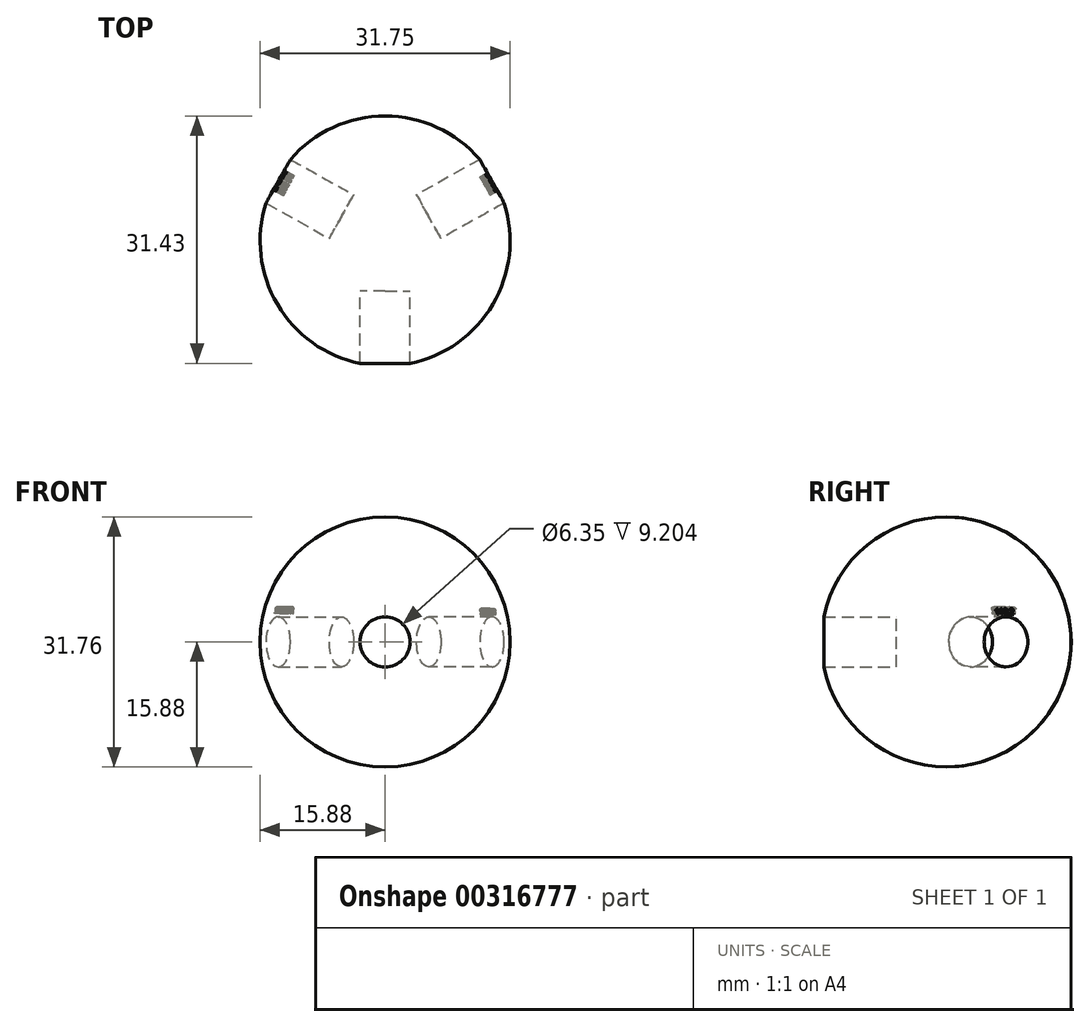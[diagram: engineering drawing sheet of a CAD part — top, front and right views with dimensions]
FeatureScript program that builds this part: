
annotation { "Feature Type Name" : "Feature", "Feature Type Description" : "" }
export const myFeature = defineFeature(function(context is Context, id is Id, definition is map)
    precondition{}
    {
        {
            var Q0;
            Q0=qCreatedBy(makeId("Front.planeOp"),FACE);
            var sketch = newSketch(context, id + "F0", { "sketchPlane" : qUnion([Q0])});
            skArc(sketch, "E0", {"start": v(0, 15.88) * mm, "mid": v(-15.88, 0) * mm, "end": v(0, -15.88) * mm});
            skLineSegment(sketch, "E1", {"start": v(0, 15.88) * mm, "end": v(0, -15.88) * mm});
            skSolve(sketch);
        }
        {
            var Q0;
            Q0=qCreatedBy(makeId("Top.planeOp"),FACE);
            var sketch = newSketch(context, id + "F1", { "sketchPlane" : qUnion([Q0])});
            skCircle(sketch, "E2", {"center": v(0, 0) * mm, "radius": 15.88 * mm});
            skSolve(sketch);
        }
        {
            var Q0;
            Q0=makeQuery(id+"F0.imprint","IMPRINT",FACE,{"disambiguationData":[TD([[makeQuery(id+"F0.imprint","IMPRINT",EDGE,{"derivedFrom":sQuery(id+"F0.wireOp",EDGE,"E0")}),1.0]])]});
            var Q1;
            Q1=sQuery(id+"F1.wireOp",EDGE,"E2");
            revolve(context, id + "F2", {"entities" : qUnion([Q0]), "axis" : qUnion([Q1]), "revolveType" : RevolveType.FULL});
        }
        {
            var Q0;
            Q0=qCreatedBy(makeId("Front.planeOp"),FACE);
            cPlane(context, id + "F3", {"entities" : qUnion([Q0]), "cplaneType" : CPlaneType.OFFSET, "offset" : 6.35 * mm, "width" : 152.4 * mm, "height" : 152.4 * mm});
        }
        {
            var Q0;
            Q0=qCreatedBy(id+"F3.planeOp",FACE);
            var sketch = newSketch(context, id + "F4", { "sketchPlane" : qUnion([Q0])});
            skCircle(sketch, "E3", {"center": v(0, 0) * mm, "radius": 3.18 * mm});
            skSolve(sketch);
        }
        {
            var Q0;
            Q0=qSketchRegion(id+"F4",true);
            extrude(context, id + "F5", {"entities" : qUnion([Q0]), "depth" : 25.4 * mm});
        }
        {
            var Q0;
            Q0=qCreatedBy(makeId("Right.planeOp"),FACE);
            var sketch = newSketch(context, id + "F6", { "sketchPlane" : qUnion([Q0])});
            skLineSegment(sketch, "E4", {"start": v(0, 67.47) * mm, "end": v(0, -53.83) * mm, "construction": true});
            skSolve(sketch);
        }
        {
            var Q0;
            Q0=makeQuery(id+"F5.opExtrude","SWEPT_BODY",BODY,{"disambiguationData":[OSD([sQuery(id+"F4.wireOp",EDGE,"E3")])]});
            var Q1;
            Q1=sQuery(id+"F6.wireOp",EDGE,"E4");
            transform(context, id + "F7", {"entities" : qUnion([Q0]), "transformType" : TransformType.ROTATION, "transformAxis" : qUnion([Q1]), "angle" : 119.2 * degree, "makeCopy" : true});
        }
        {
            var Q0;
            Q0=makeQuery(id+"F5.opExtrude","SWEPT_BODY",BODY,{"disambiguationData":[OSD([sQuery(id+"F4.wireOp",EDGE,"E3")])]});
            var Q1;
            Q1=sQuery(id+"F6.wireOp",EDGE,"E4");
            transform(context, id + "F8", {"entities" : qUnion([Q0]), "transformType" : TransformType.ROTATION, "transformAxis" : qUnion([Q1]), "angle" : 119.2 * degree, "oppositeDirection" : true, "makeCopy" : true});
        }
        {
            var Q0;
            Q0=makeQuery(id+"F7.opPattern","COPY",FACE,{"derivedFrom":makeQuery(id+"F5.opExtrude","CAP_FACE",FACE,{"disambiguationData":[OSD([sQuery(id+"F4.wireOp",EDGE,"E3")])],"isStart":false}),"instanceName":"1"});
            cPlane(context, id + "F9", {"entities" : qUnion([Q0]), "cplaneType" : CPlaneType.OFFSET, "offset" : 15.21 * mm, "oppositeDirection" : true, "width" : 152.4 * mm, "height" : 152.4 * mm});
        }
        {
            var Q0;
            Q0=qCreatedBy(id+"F9.planeOp",FACE);
            var sketch = newSketch(context, id + "F10", { "sketchPlane" : qUnion([Q0])});
            skText(sketch, "E5", { "text": "119.2", "fontName": "OpenSans-Bold.ttf"});
            const initialGuessF10  = {"E5": [-0.00169, 0.00362, 1, 0, 0.00084]};
            skSetInitialGuess(sketch, initialGuessF10);
            skSolve(sketch);
        }
        {
            var Q0;
            Q0 = qSketchRegion(id + "F10", true);
            extrude(context, id + "F11", {"entities" : qUnion([Q0]), "operationType" : NewBodyOperationType.REMOVE, "oppositeDirection" : true, "depth" : 2.41 * mm});
        }
        {
            var Q0;
            Q0=makeQuery(id+"F8.opPattern","COPY",FACE,{"derivedFrom":makeQuery(id+"F5.opExtrude","CAP_FACE",FACE,{"disambiguationData":[OSD([sQuery(id+"F4.wireOp",EDGE,"E3")])],"isStart":false}),"instanceName":"1"});
            cPlane(context, id + "F12", {"entities" : qUnion([Q0]), "cplaneType" : CPlaneType.OFFSET, "offset" : 15.14 * mm, "oppositeDirection" : true, "width" : 152.4 * mm, "height" : 152.4 * mm});
        }
        {
            var Q0;
            Q0=qCreatedBy(id+"F12.planeOp",FACE);
            var sketch = newSketch(context, id + "F13", { "sketchPlane" : qUnion([Q0])});
            skText(sketch, "E6", { "text": "119.2", "fontName": "OpenSans-Bold.ttf"});
            const initialGuessF13  = {"E6": [-0.00147, 0.00348, 1, 0, 0.00076]};
            skSetInitialGuess(sketch, initialGuessF13);
            skSolve(sketch);
        }
        {
            var Q0;
            Q0 = qSketchRegion(id + "F13", true);
            extrude(context, id + "F14", {"entities" : qUnion([Q0]), "operationType" : NewBodyOperationType.REMOVE, "oppositeDirection" : true, "depth" : 2.1 * mm});
        }
        {
            var Q0;
            Q0=makeQuery(id+"F7.opPattern","COPY",BODY,{"derivedFrom":makeQuery(id+"F5.opExtrude","SWEPT_BODY",BODY,{"disambiguationData":[OSD([sQuery(id+"F4.wireOp",EDGE,"E3")])]}),"instanceName":"1"});
            var Q1;
            Q1=makeQuery(id+"F2.opRevolve","SWEPT_BODY",BODY,{"disambiguationData":[OSD([sQuery(id+"F0.wireOp",EDGE,"E0"),sQuery(id+"F0.wireOp",EDGE,"E1")])]});
            booleanBodies(context, id + "F15", {"operationType" : BooleanOperationType.SUBTRACTION, "tools" : qUnion([Q0]), "targets" : qUnion([Q1])});
        }
        {
            var Q0;
            Q0=makeQuery(id+"F8.opPattern","COPY",BODY,{"derivedFrom":makeQuery(id+"F5.opExtrude","SWEPT_BODY",BODY,{"disambiguationData":[OSD([sQuery(id+"F4.wireOp",EDGE,"E3")])]}),"instanceName":"1"});
            var Q1;
            Q1=makeQuery(id+"F2.opRevolve","SWEPT_BODY",BODY,{"disambiguationData":[OSD([sQuery(id+"F0.wireOp",EDGE,"E0"),sQuery(id+"F0.wireOp",EDGE,"E1")])]});
            booleanBodies(context, id + "F16", {"operationType" : BooleanOperationType.SUBTRACTION, "tools" : qUnion([Q0]), "targets" : qUnion([Q1])});
        }
        {
            var Q0;
            Q0=makeQuery(id+"F5.opExtrude","SWEPT_BODY",BODY,{"disambiguationData":[OSD([sQuery(id+"F4.wireOp",EDGE,"E3")])]});
            var Q1;
            Q1=makeQuery(id+"F2.opRevolve","SWEPT_BODY",BODY,{"disambiguationData":[OSD([sQuery(id+"F0.wireOp",EDGE,"E0"),sQuery(id+"F0.wireOp",EDGE,"E1")])]});
            booleanBodies(context, id + "F17", {"operationType" : BooleanOperationType.SUBTRACTION, "tools" : qUnion([Q0]), "targets" : qUnion([Q1])});
        }
    });
